# Revit family: Legrand_Lighting_Management_Standalone_Motion_Sensor_Ceiling
name_source: partatom
category: Dispositifs d'éclairage
units: mm (PartAtom-declared; Revit-internal decimal feet)

## family parameters
Conserver l'orientation des annotations = Non
Cote de connecteur circulaire = Utiliser le diamètre
Couper avec des vides une fois chargée = Non
Hôte = Face
Partagée = Non
Point de calcul de pièce = Non
Type d'élément = Normal

## types (2) — shared parameters
Alarm function = Non
Collecteur de terre = Non
Colour = White
Constant light control = Oui
Cosses d'artère secondaire = Non
Detection angle horizontal (MAX) (°) = 360
Diameter detection range on floor (m) = 8
Dim function with dimmer basic element = Non
Elévation par défaut = 1219 mm
Fabricant = Legrand
Forced switch off = Non
Frequency (MAX) (Hz) = 60
Frequency (MIN) (Hz) = 50
General Conditions of Use = https://export.legrand.com
HVAC-control = Non
Liaison neutre = Non
Maximum mounting height (m) = 2.5
Remote operation = Non
Response value luminosity (MAX) (lx) = 1275
Response value luminosity adjustable = Oui
Substation input = Non
Suitable for wireless transmission = Non
URL = http://www.legrandoc.com
Voltage type = AC

## per-type parameters (varying)
| type | Classe de protection (IP) | Description | Detection angle horizontal (MIN) (°) | Max. duty cycle (mn) | Max. starting current (A) | Max. switching power (W) | Max. transmission range frontally (m) | Max. transmission range sideways (m) | Min. switch-on time (s) | Model | Modèle | Mounting method | Nominal voltage (V) | RAL-number (akin) | Response value luminosity (MIN) (lx) | Response value sensitivity adjustable | Temperature (MAX) (°C) | Temperature (MIN) (°C) |
| PIR - Surface - 360° - 45m² | IP20 | PIR 360° SENSOR CEILING SURFACE MOUNTED | 360 | 10 | 0 | 0 | 8 | 8 | 10 | Presence detector | 048948 | Surface mounted (plaster) | 240 | 9006 | 10 | Oui | -5 | 35 |
| PIR - Recessed - 360° - 45m² | IP41 | PACK CEILING DETECTOR | 0 | 30 | 8.5 | 2000 | 6 | 4 | 5 | Movement sensor | 048899 | Flush mounted (plaster) | 230 | 9003 | 5 | Non | 45 | -5 |
